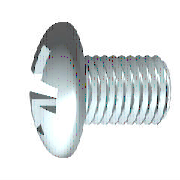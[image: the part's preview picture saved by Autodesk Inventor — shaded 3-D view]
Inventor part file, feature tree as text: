
AUTODESK INVENTOR PART (.ipt)
format: ipt  version: 2020 (Build 240168000, 168)  size: 268,288 bytes
history: native  units: mm (DEFAULTED — no unit token found)
features: extrude x1, other x1, plane x1
ambient origin geometry x7: Origin, YZ Plane, XZ Plane, X Axis, Y Axis, Z Axis, Center Point
bodies: Solid1 (feature_tree), Body (feature_tree)
feature tree (3):
  extrude  "Slot"  Depth=2.0mm
  other  "Cut"
  plane  "Work Plane3"
